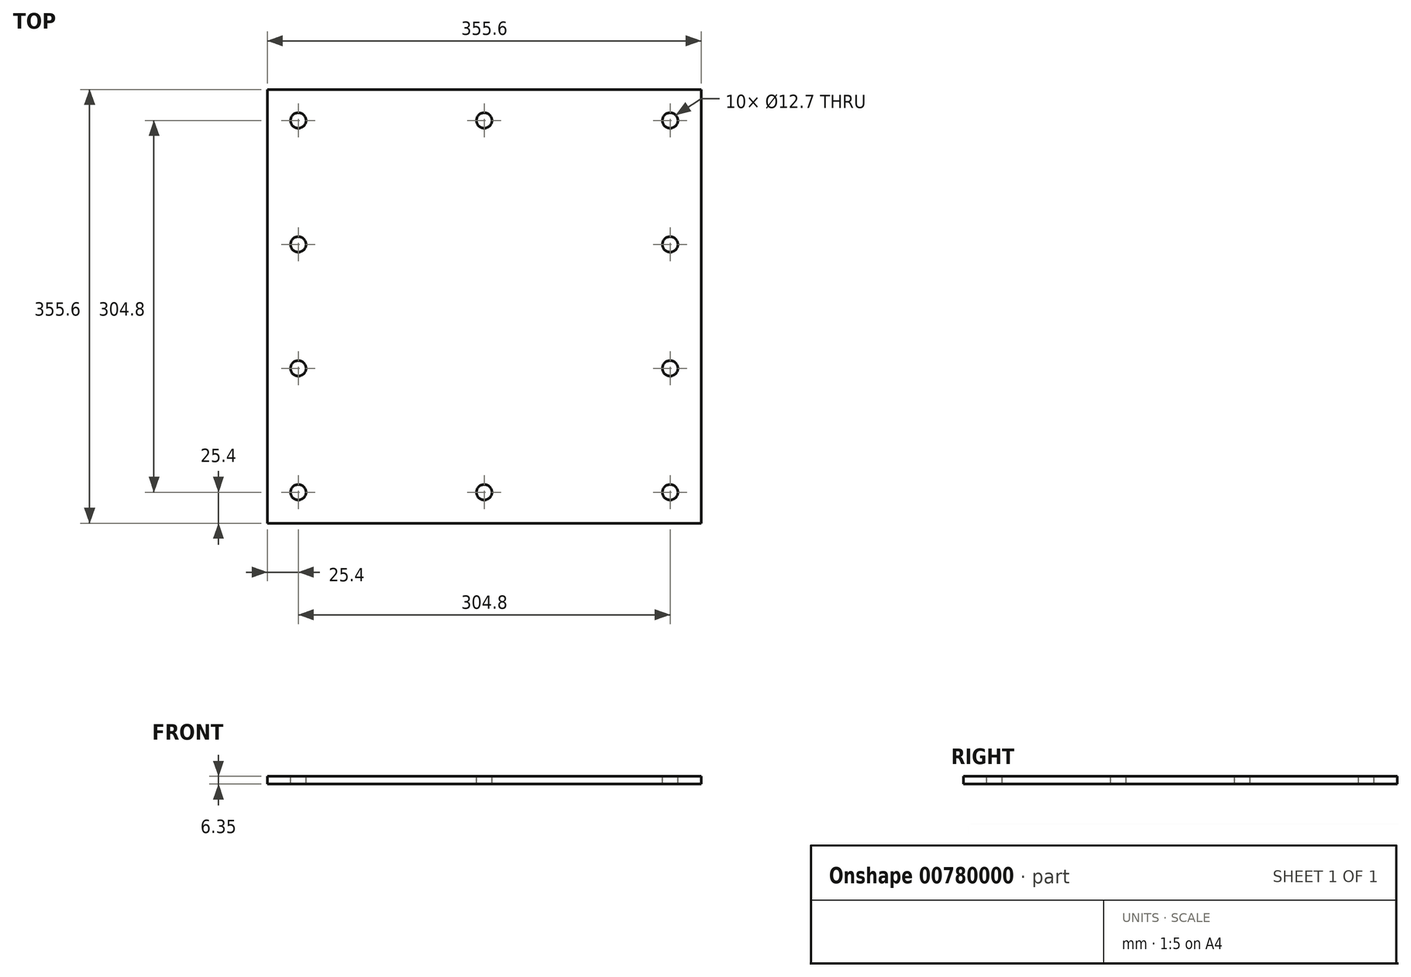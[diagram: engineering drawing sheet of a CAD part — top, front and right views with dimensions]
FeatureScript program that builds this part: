
annotation { "Feature Type Name" : "Feature", "Feature Type Description" : "" }
export const myFeature = defineFeature(function(context is Context, id is Id, definition is map)
    precondition{}
    {
        {
            var Q0;
            Q0=qCreatedBy(makeId("Top.planeOp"),FACE);
            var sketch = newSketch(context, id + "F0", { "sketchPlane" : qUnion([Q0])});
            skLineSegment(sketch, "E0.bottom", {"start": v(0, 0) * mm, "end": v(355.6, 0) * mm});
            skLineSegment(sketch, "E0.top", {"start": v(0, 355.6) * mm, "end": v(355.6, 355.6) * mm});
            skLineSegment(sketch, "E0.left", {"start": v(0, 0) * mm, "end": v(0, 355.6) * mm});
            skLineSegment(sketch, "E0.right", {"start": v(355.6, 0) * mm, "end": v(355.6, 355.6) * mm});
            skSolve(sketch);
        }
        {
            var Q0;
            Q0=makeQuery(id+"F0.imprint","IMPRINT",FACE,{"disambiguationData":[TD([[makeQuery(id+"F0.imprint","IMPRINT",EDGE,{"derivedFrom":sQuery(id+"F0.wireOp",EDGE,"E0.bottom")}),1.0]])]});
            extrude(context, id + "F1", {"entities" : qUnion([Q0]), "depth" : 6.35 * mm, "offsetDistance" : 25.4 * mm});
        }
        {
            var Q0;
            Q0=makeQuery(id+"F1.opExtrude","CAP_FACE",FACE,{"disambiguationData":[OSD([sQuery(id+"F0.wireOp",EDGE,"E0.bottom"),sQuery(id+"F0.wireOp",EDGE,"E0.top"),sQuery(id+"F0.wireOp",EDGE,"E0.left"),sQuery(id+"F0.wireOp",EDGE,"E0.right")])],"isStart":false});
            var sketch = newSketch(context, id + "F2", { "sketchPlane" : qUnion([Q0])});
            skLineSegment(sketch, "E1", {"start": v(25.4, 355.6) * mm, "end": v(25.4, 0) * mm, "construction": true});
            skLineSegment(sketch, "E2", {"start": v(0, 177.8) * mm, "end": v(355.6, 177.8) * mm, "construction": true});
            skCircle(sketch, "E3", {"center": v(25.4, 228.6) * mm, "radius": 6.35 * mm});
            skCircle(sketch, "E4", {"center": v(177.8, 330.2) * mm, "radius": 6.35 * mm});
            skCircle(sketch, "E5", {"center": v(330.2, 228.6) * mm, "radius": 6.35 * mm});
            skCircle(sketch, "E6.MirrorC", {"center": v(25.4, 127) * mm, "radius": 6.35 * mm});
            skCircle(sketch, "E7.MirrorC", {"center": v(177.8, 25.4) * mm, "radius": 6.35 * mm});
            skCircle(sketch, "E8.MirrorC", {"center": v(330.2, 127) * mm, "radius": 6.35 * mm});
            skSolve(sketch);
        }
        {
            var Q0;
            Q0 = qSketchRegion(id + "F2", true);
            extrude(context, id + "F3", {"entities" : qUnion([Q0]), "operationType" : NewBodyOperationType.REMOVE, "oppositeDirection" : true, "depth" : 25.4 * mm, "offsetDistance" : 25.4 * mm});
        }
        {
            var Q0;
            Q0=makeQuery(id+"F1.opExtrude","CAP_FACE",FACE,{"disambiguationData":[OSD([sQuery(id+"F0.wireOp",EDGE,"E0.bottom"),sQuery(id+"F0.wireOp",EDGE,"E0.top"),sQuery(id+"F0.wireOp",EDGE,"E0.left"),sQuery(id+"F0.wireOp",EDGE,"E0.right")])],"isStart":false});
            var sketch = newSketch(context, id + "F4", { "sketchPlane" : qUnion([Q0])});
            skSolve(sketch);
        }
        {
            var Q0;
            Q0=makeQuery(id+"F4.imprint","IMPRINT",FACE,{"disambiguationData":[TD([[makeQuery(id+"F4.imprint","IMPRINT",EDGE,{"derivedFrom":makeQuery(id+"F1.opExtrude","CAP_EDGE",EDGE,{"disambiguationData":[OSD([sQuery(id+"F0.wireOp",EDGE,"E0.bottom")])],"isStart":false})}),1.0]])]});
            var sketch = newSketch(context, id + "F5", { "sketchPlane" : qUnion([Q0])});
            skLineSegment(sketch, "E9", {"start": v(0, 177.8) * mm, "end": v(355.6, 177.8) * mm, "construction": true});
            skLineSegment(sketch, "E10", {"start": v(177.8, 0) * mm, "end": v(177.8, 356.34) * mm, "construction": true});
            skPoint(sketch, "E10.startSnap0", {"position": v(177.8, 177.8) * mm});
            skPoint(sketch, "E10.endSnap0", {"position": v(177.8, 177.8) * mm});
            skCircle(sketch, "E11", {"center": v(25.4, 330.2) * mm, "radius": 6.35 * mm});
            skCircle(sketch, "E12.MirrorC", {"center": v(330.2, 330.2) * mm, "radius": 6.35 * mm});
            skCircle(sketch, "E13.MirrorC", {"center": v(25.4, 25.4) * mm, "radius": 6.35 * mm});
            skCircle(sketch, "E14.MirrorC", {"center": v(330.2, 25.4) * mm, "radius": 6.35 * mm});
            skSolve(sketch);
        }
        {
            var Q0;
            Q0 = qSketchRegion(id + "F5", true);
            extrude(context, id + "F6", {"entities" : qUnion([Q0]), "operationType" : NewBodyOperationType.REMOVE, "oppositeDirection" : true, "depth" : 25.4 * mm, "offsetDistance" : 25.4 * mm});
        }
    });
